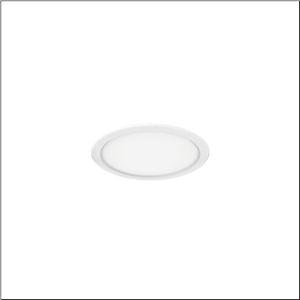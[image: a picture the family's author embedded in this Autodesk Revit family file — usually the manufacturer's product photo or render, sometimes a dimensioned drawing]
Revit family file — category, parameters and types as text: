
# Revit family: lunis_41_eco_51ds107d33b
name_source: partatom
category: Lighting Fixtures
units: mm (PartAtom-declared; Revit-internal decimal feet)

## family parameters
Cut with Voids When Loaded = No
Host = Face
Light Source = No
Part Type = Normal
Room Calculation Point = No
Round Connector Dimension = Use Diameter
Shared = No

## types (1)
- Lunis 41 Eco (1 x LED, 1460 lm, 12 W, 3000K)
    Apparent Load = 12 VA
    CIE Flux Codes = 47 80 97 100 100
    Color Rendering = 80
    Color Temperature = 3000K
    Default Elevation = 1800 mm
    Description = Lunis 41 Eco, downlight, light emission: direct distribution, LED rated luminous flux: 1.460lm, light colour: 830, mains connection: 230V, AC, 50/60Hz, housing, round, of aluminium, coated, traffic white (RAL 9016), diameter: 166mm, recess depth: 54mm, protection rating (complete): IP20, protection rating (on room side): IP40, insulation class (complete): insulation class II (safety insulation), certification: CE, permissible ambient temperature for indoor applications: -20..+40°C, packaging unit: 1 piece
    Height = 0 mm  [stored 0 ft]
    Lamp = 1 x LED
    Lamp Light Flux = 1460 lm
    Lamp Power = 12 W
    Lamp count = 1
    Length = 166 mm
    Luminous efficacy = 122 lm/W
    Manufacturer = Siteco
    ModVariant = No
    Model = 51DS107D33B
    Mounting Place = Ceiling
    Mounting Type = Recessed
    Number of Poles = 1
    OnlyDefault = Yes
    Power Factor = 1
    Product Name = Lunis 41 Eco
    Product group = downlight
    ProductGroupID = 401
    Protection Class = Protection class II
    Protection Degree = IP 20
    RLX_Detail_Level = 1
    RLX_Emergency_Light_Flux = 0 lm
    RLX_Emergency_Type = 0
    RLX_Emergency_Type_DB = No
    RlxData = <blob elided: 8893 chars, md5=88217ebc>
    Socket = socket
    Standby Power = 0 W
    System Light Flux = 1460 lm
    System Power = 12 W
    Type Comments = Product without accessories
    Type Image = l_1345912.jpg
    URL = http://relux.com
    VarID = ---
    Voltage = 0 V
    Weight = 0.00 kg
    Width = 0 mm  [stored 0 ft]

note: [stored X ft] marks values corroborated as IEEE doubles in the binary element streams (Revit-internal decimal feet)

## geometry (parser evidence)
native form markers: Sweep x10
no freeform markers — native parametric forms only
